# Revit family: Rundstahlbügel, Ø273-323,9
name_source: partatom
category: HLS-Bauteile
revit_build: Autodesk Revit 2018 (Build: 20190510_1515(x64)
units: mm (PartAtom-declared; Revit-internal decimal feet)

## family parameters
Arbeitsebenenbasiert = Ja
Beim Laden mit Abzugskörper schneiden = Nein
Bemaßung runder Anschluss = Durchmesser verwenden
Gemeinsam genutzt = Ja
Immer vertikal = Nein
Raumberechnungspunkt = Nein
Teiletyp = Normal

## types (2) — shared parameters
B = 70 mm  [stored 0.229659 ft]
Fabrikat = MEFA
Firma = MEFA Befestigungs- und Montagesysteme GmbH
Gewinde = M20
Kurztext1 = Rundstahlbügel
Länge Gewinde = 70 mm  [stored 0.229659 ft]
M = 20 mm  [stored 0.0656168 ft]
Material = Stahl
Materialname = S235
Mengeneinheit = St
Oberflaeche = galvanisch verzinkt
Vorgabe-Ansicht = 1219 mm
d2 = 19 mm
zero-valued in all types: Nennweite DN Rohr, max. Profilhöhe

## per-type parameters (varying)
| type | A | Achsabstand | Artikelnummer | EAN | Gewicht | Gewicht pro Bauteil | H | Höhe | Kurztext2 | L1 | Rohraußendurchmesser | Rohraußendurchmesser Zoll | vpe |
| Rundstahlbügel, M20, Ø273 | 302 mm | 302 mm | 0507273 | 4250928414373 | 1.66 kg | 1.66 kg | 313 mm | 313 mm | 273 mm M20 Gesamthöhe 313 mm | 101 mm | 273 mm | 10 Zoll | 10 St |
| Rundstahlbügel, M20, Ø323,9 | 352 mm  [stored 1.15486 ft] | 352 mm | 0507324 | 4250928414380 | 1.93 kg | 1.93 kg | 364 mm | 364 mm | 323.9 mm M20 Gesamthöhe 364 mm | 127 mm | 324 mm | 12 Zoll | 1 St |

note: [stored X ft] marks values corroborated as IEEE doubles in the binary element streams (Revit-internal decimal feet)
